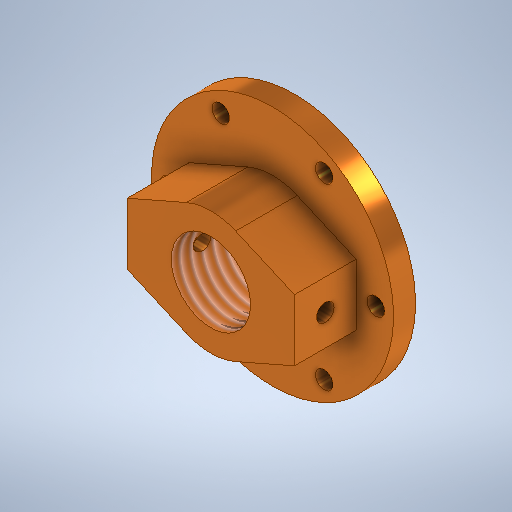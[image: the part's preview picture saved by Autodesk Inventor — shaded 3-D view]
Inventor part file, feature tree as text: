
AUTODESK INVENTOR PART (.ipt)
format: ipt  version: 2025.1 (Build 291241000, 241)  size: 359,936 bytes
history: native  units: mm
features: sketch x7, extrude x5, hole x2, pattern_circular x1, thread x1, mirror x1
ambient origin geometry x8: Origin, YZ Plane, XZ Plane, XY Plane, X Axis, Y Axis, Z Axis, Center Point
bodies: Volumenkörper1 (feature_tree)
feature tree (17):
  extrude  "Extrusion1"  Depth=5.0mm TaperAngle=0.0deg
  extrude  "Extrusion2"  Depth=1.5mm TaperAngle=0.0deg
  extrude  "Extrusion3"  Depth=10.0mm
  hole  "Bohrung1"  [1 undecoded]
  pattern_circular  "Runde Anordnung1"  Count=6 Angle=360.0deg
  extrude  "Extrusion4"  Depth=10.0mm
  extrude  "Extrusion5"  Depth=10.0mm
  thread  "Gewinde1"  [1 undecoded]
  hole  "Bohrung2"  [1 undecoded]
  mirror  "Mirror1"
  sketch  "Skizze1"  dims[d0=55.0mm d2=5.0mm d3=0.0mm]
  sketch  "Skizze2"  dims[d4=30.0mm d5=1.5mm d6=0.0mm]
  sketch  "Skizze3"  dims[d7=13.0mm d8=10.0mm]
  sketch  "Skizze4"  dims[d9=2.0mm d10=1.5mm d11=0.0mm]
  sketch  "Skizze5"  dims[d12=47.0mm]
  sketch  "Skizze6"  dims[d13=4.0mm d14=6.0mm d15=4.0mm d16=2.0mm d17=90.0deg d18=8.0mm d19=20.594885mm d20=60.0mm d21=360.0deg]
  sketch  "Skizze7"  dims[d25=28.0mm d27=14.0mm d28=14.0mm d29=38.0mm d30=14.0mm d31=0.0mm d32=18.0mm d33=15.5mm d34=0.0mm d35=14.0mm d36=0.0mm d37=4.0mm d38=6.0mm d39=4.0mm d40=2.0mm d41=90.0deg d42=10.0mm d43=20.594885mm]
note: 3 required parameter values undecoded (feature->parameter linkage not recoverable at this tier; creation-order binding heuristic only, values carry confidence <= 0.55)
